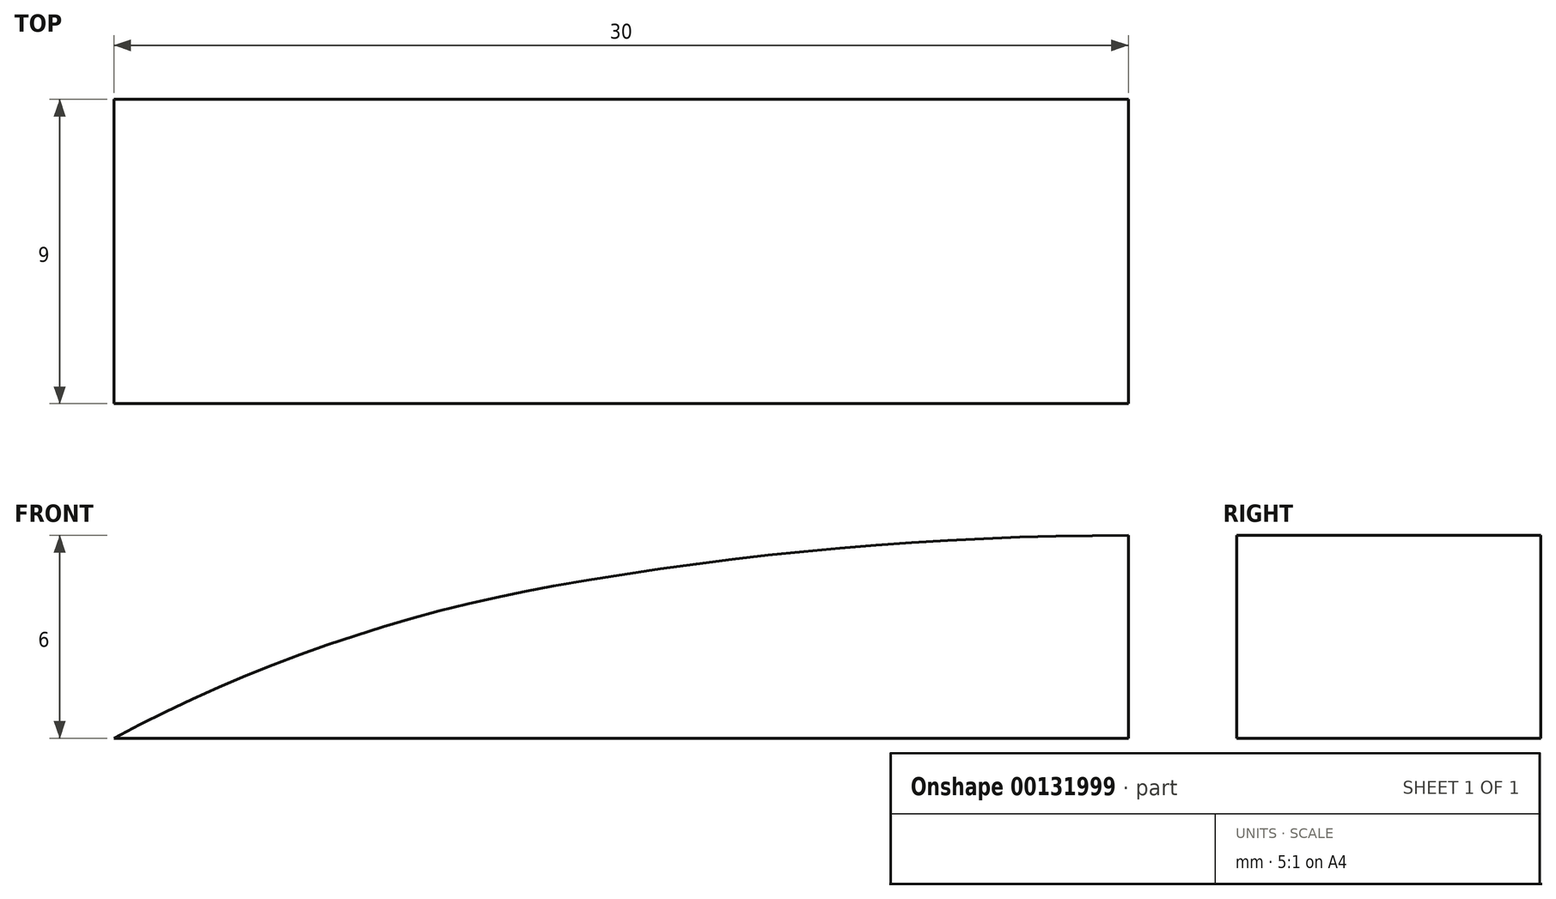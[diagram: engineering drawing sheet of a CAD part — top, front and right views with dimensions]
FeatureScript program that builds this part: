
annotation { "Feature Type Name" : "Feature", "Feature Type Description" : "" }
export const myFeature = defineFeature(function(context is Context, id is Id, definition is map)
    precondition{}
    {
        {
            var Q0;
            Q0=qCreatedBy(makeId("Front.planeOp"),FACE);
            var sketch = newSketch(context, id + "F0", { "sketchPlane" : qUnion([Q0])});
            skLineSegment(sketch, "E0", {"start": v(0, 0) * mm, "end": v(30, 0) * mm});
            skLineSegment(sketch, "E1", {"start": v(30, 0) * mm, "end": v(30, 6) * mm});
            skLineSegment(sketch, "E2", {"start": v(30, 6) * mm, "end": v(40.04, 6) * mm, "construction": true});
            skLineSegment(sketch, "E3", {"start": v(13, 0) * mm, "end": v(13, 4.5) * mm, "construction": true});
            skArc(sketch, "E4", {"start": v(30, 6) * mm, "mid": v(21.47, 5.62) * mm, "end": v(13, 4.5) * mm});
            skArc(sketch, "E5", {"start": v(13, 4.5) * mm, "mid": v(6.32, 2.76) * mm, "end": v(0, 0) * mm});
            skSolve(sketch);
        }
        {
            var Q0;
            Q0 = qSketchRegion(id + "F0", true);
            extrude(context, id + "F1", {"entities" : qUnion([Q0]), "depth" : 9 * mm});
        }
    });
